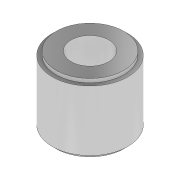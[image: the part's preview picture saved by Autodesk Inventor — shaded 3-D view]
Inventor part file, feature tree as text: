
AUTODESK INVENTOR PART (.ipt)
format: ipt  version: 2020 (Build 240168000, 168)  size: 121,344 bytes
history: native  units: in
note: dims shown in document units (in); Inventor stores cm internally (conversion verified against a paired STEP export)
features: extrude x5, sketch x5, projected_geometry x1
ambient origin geometry x8: Origin, YZ Plane, XZ Plane, XY Plane, X Axis, Y Axis, Z Axis, Center Point
bodies: Solid1 (feature_tree)
feature tree (11):
  extrude  "Extrusion1"  Depth=0.1969in
  extrude  "Extrusion2"  Depth=0.3937in
  extrude  "Extrusion3"  Depth=0.0197in TaperAngle=0.0deg
  extrude  "Extrusion4"  Depth=0.0197in TaperAngle=0.0deg
  extrude  "Extrusion5"  [1 undecoded]
  sketch  "Sketch1"  dims[d0=0.7087in d1=0.1969in]
  sketch  "Sketch2"  dims[d2=0.0197in d3=0.0in d4=0.3937in]
  sketch  "Sketch3"  dims[d5=0.315in d6=0.0in d7=0.0197in d8=0.0in]
  sketch  "Sketch4"  dims[d9=0.0197in d10=1.0in d11=0.0in]
  projected_geometry  "Projected Loop1"
  sketch  "Sketch5"  dims[d12=1.0in d13=0.0in]
note: 1 required parameter value undecoded (feature->parameter linkage not recoverable at this tier; creation-order binding heuristic only, values carry confidence <= 0.55)
